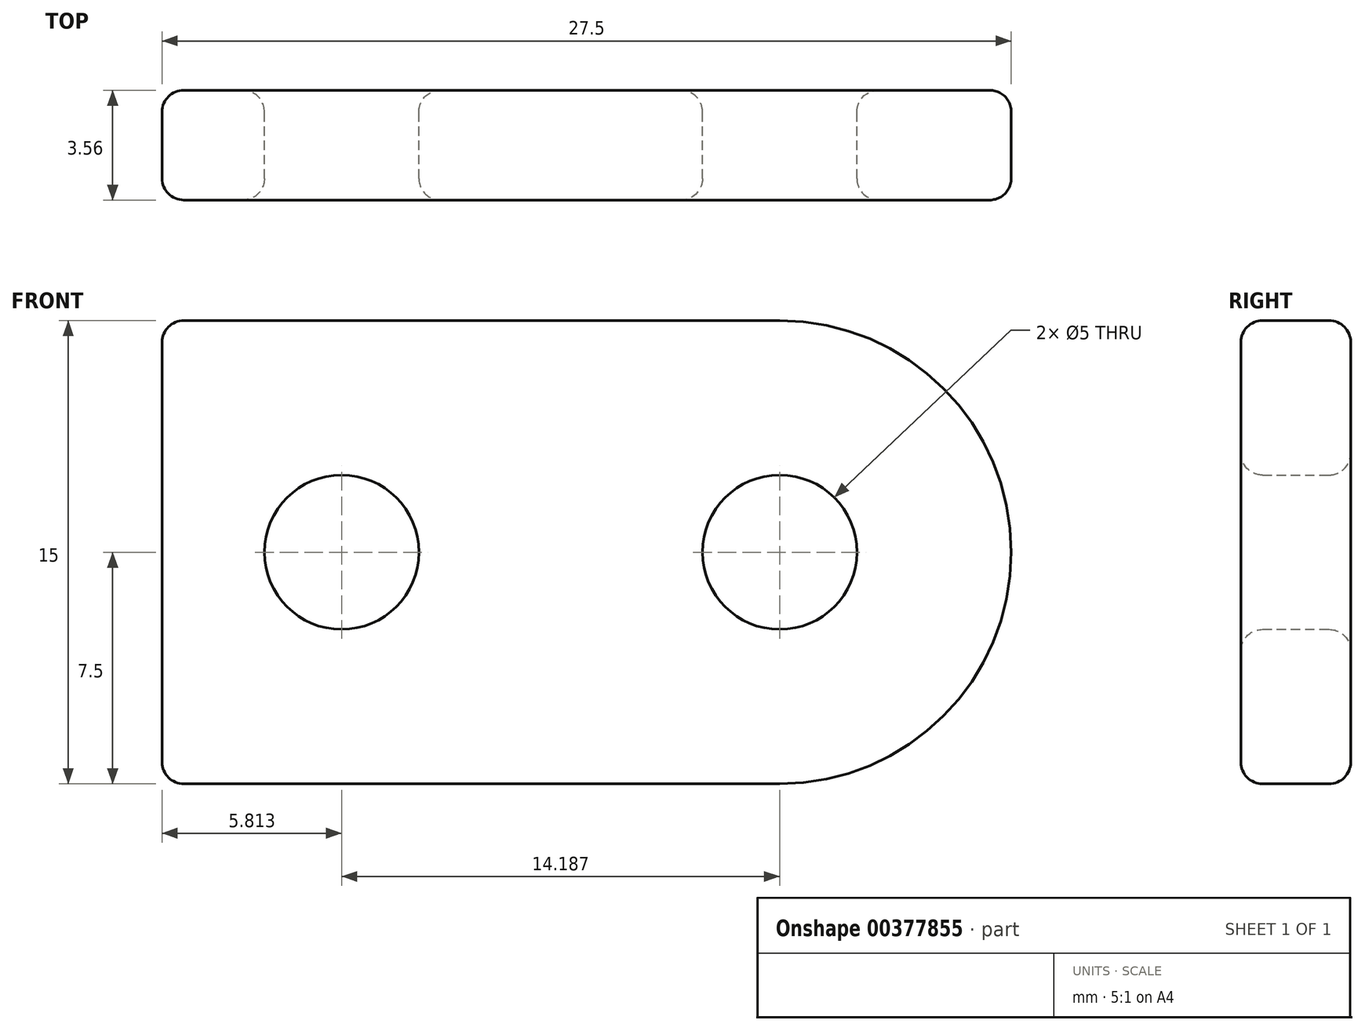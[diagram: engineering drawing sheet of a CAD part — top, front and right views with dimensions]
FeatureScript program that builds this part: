
annotation { "Feature Type Name" : "Feature", "Feature Type Description" : "" }
export const myFeature = defineFeature(function(context is Context, id is Id, definition is map)
    precondition{}
    {
        {
            var Q0;
            Q0=qCreatedBy(makeId("Front.planeOp"),FACE);
            var sketch = newSketch(context, id + "F0", { "sketchPlane" : qUnion([Q0])});
            skLineSegment(sketch, "E0.bottom", {"start": v(-20, 7.5) * mm, "end": v(0, 7.5) * mm});
            skLineSegment(sketch, "E0.top", {"start": v(-20, -7.5) * mm, "end": v(0, -7.5) * mm});
            skLineSegment(sketch, "E0.left", {"start": v(-20, 7.5) * mm, "end": v(-20, -7.5) * mm});
            skArc(sketch, "E1", {"start": v(0, -7.5) * mm, "mid": v(7.5, 0) * mm, "end": v(0, 7.5) * mm});
            skCircle(sketch, "E2", {"center": v(-14.19, 0) * mm, "radius": 2.5 * mm});
            skPoint(sketch, "E2.centerSnap0", {"position": v(-20, 0) * mm});
            skPoint(sketch, "E2.perimeterSnap0", {"position": v(-10, -7.5) * mm});
            skPoint(sketch, "E2.perimeterSnap1", {"position": v(7.5, 0) * mm});
            skCircle(sketch, "E3", {"center": v(0, 0) * mm, "radius": 2.5 * mm});
            skSolve(sketch);
        }
        {
            var Q0;
            Q0=makeQuery(id+"F0.imprint","IMPRINT",FACE,{"disambiguationData":[TD([[makeQuery(id+"F0.imprint","IMPRINT",EDGE,{"derivedFrom":sQuery(id+"F0.wireOp",EDGE,"E0.bottom")}),-1.0]])]});
            extrude(context, id + "F1", {"entities" : qUnion([Q0]), "depth" : 3.56 * mm});
        }
        {
            var Q0;
            Q0=makeQuery(id+"F1.opExtrude","CAP_EDGE",EDGE,{"disambiguationData":[OSD([sQuery(id+"F0.wireOp",EDGE,"E2")])],"isStart":false});
            var Q1;
            Q1=makeQuery(id+"F1.opExtrude","CAP_EDGE",EDGE,{"disambiguationData":[OSD([sQuery(id+"F0.wireOp",EDGE,"E3")])],"isStart":false});
            var Q2;
            Q2=makeQuery(id+"F1.opExtrude","CAP_EDGE",EDGE,{"disambiguationData":[OSD([sQuery(id+"F0.wireOp",EDGE,"E0.top")])],"isStart":false});
            var Q3;
            Q3=makeQuery(id+"F1.opExtrude","CAP_EDGE",EDGE,{"disambiguationData":[OSD([sQuery(id+"F0.wireOp",EDGE,"E1")])],"isStart":false});
            var Q4;
            Q4=makeQuery(id+"F1.opExtrude","CAP_EDGE",EDGE,{"disambiguationData":[OSD([sQuery(id+"F0.wireOp",EDGE,"E0.bottom")])],"isStart":false});
            var Q5;
            Q5=makeQuery(id+"F1.opExtrude","CAP_EDGE",EDGE,{"disambiguationData":[OSD([sQuery(id+"F0.wireOp",EDGE,"E0.left")])],"isStart":false});
            var Q6;
            Q6=makeQuery(id+"F1.opExtrude","SWEPT_EDGE",EDGE,{"disambiguationData":[OSD([sQuery(id+"F0.wireOp",EDGE,"E0.bottom"),sQuery(id+"F0.wireOp",EDGE,"E0.left")])]});
            var Q7;
            Q7=makeQuery(id+"F1.opExtrude","SWEPT_EDGE",EDGE,{"disambiguationData":[OSD([sQuery(id+"F0.wireOp",EDGE,"E0.top"),sQuery(id+"F0.wireOp",EDGE,"E0.left")])]});
            var Q8;
            Q8=makeQuery(id+"F1.opExtrude","CAP_EDGE",EDGE,{"disambiguationData":[OSD([sQuery(id+"F0.wireOp",EDGE,"E0.top")])],"isStart":true});
            var Q9;
            Q9=makeQuery(id+"F1.opExtrude","CAP_EDGE",EDGE,{"disambiguationData":[OSD([sQuery(id+"F0.wireOp",EDGE,"E0.left")])],"isStart":true});
            var Q10;
            Q10=makeQuery(id+"F1.opExtrude","CAP_EDGE",EDGE,{"disambiguationData":[OSD([sQuery(id+"F0.wireOp",EDGE,"E0.bottom")])],"isStart":true});
            var Q11;
            Q11=makeQuery(id+"F1.opExtrude","CAP_EDGE",EDGE,{"disambiguationData":[OSD([sQuery(id+"F0.wireOp",EDGE,"E2")])],"isStart":true});
            var Q12;
            Q12=makeQuery(id+"F1.opExtrude","CAP_EDGE",EDGE,{"disambiguationData":[OSD([sQuery(id+"F0.wireOp",EDGE,"E3")])],"isStart":true});
            var Q13;
            Q13=makeQuery(id+"F1.opExtrude","CAP_EDGE",EDGE,{"disambiguationData":[OSD([sQuery(id+"F0.wireOp",EDGE,"E1")])],"isStart":true});
            fillet(context, id + "F2", {"entities" : qUnion([Q0, Q1, Q2, Q3, Q4, Q5, Q6, Q7, Q8, Q9, Q10, Q11, Q12, Q13]), "radius" : 0.7 * mm, "tangentPropagation" : true, "allowEdgeOverflow" : false});
        }
    });
